FCSTD DOCUMENT  (FreeCAD 0.19R24276 (Git))
Label: Master_sketch_3_3
License: All rights reserved
LicenseURL: http://en.wikipedia.org/wiki/All_rights_reserved
objects: Sketcher::SketchObject×1, PartDesign::Body×1
note: 2 computed .brp shape members not serialized (recipe doc carries the construction recipe); baked Part::Feature solids carry a one-line shape summary decoded from their .brp

FEATURE [Sketcher::SketchObject] Sketch
  FullyConstrained = false
  MapMode = 5
  Support = -> [XY_Plane]
  sketch-geometry (226):
    g0: LineSegment StartX=-40 StartY=82 StartZ=0 EndX=40 EndY=82 EndZ=0
    g1: LineSegment StartX=40 StartY=82 StartZ=0 EndX=40 EndY=71 EndZ=0
    g2: LineSegment StartX=40 StartY=71 StartZ=0 EndX=-40 EndY=71 EndZ=0
    g3: LineSegment StartX=-40 StartY=71 StartZ=0 EndX=-40 EndY=82 EndZ=0
    g4: LineSegment StartX=-25 StartY=82 StartZ=0 EndX=-25 EndY=71 EndZ=0
    g5: LineSegment StartX=25 StartY=82 StartZ=0 EndX=25 EndY=71 EndZ=0
    g6: LineSegment StartX=-40 StartY=71 StartZ=0 EndX=-25 EndY=82 EndZ=0
    g7: LineSegment StartX=-40 StartY=82 StartZ=0 EndX=-25 EndY=71 EndZ=0
    g8: LineSegment StartX=25 StartY=71 StartZ=0 EndX=40 EndY=82 EndZ=0
    g9: LineSegment StartX=25 StartY=82 StartZ=0 EndX=40 EndY=71 EndZ=0
    g10: LineSegment StartX=-40 StartY=104 StartZ=0 EndX=40 EndY=104 EndZ=0
    g11: LineSegment StartX=40 StartY=104 StartZ=0 EndX=40 EndY=115 EndZ=0
    g12: LineSegment StartX=40 StartY=115 StartZ=0 EndX=-40 EndY=115 EndZ=0
    g13: LineSegment StartX=-40 StartY=115 StartZ=0 EndX=-40 EndY=104 EndZ=0
    g14: LineSegment StartX=-25 StartY=104 StartZ=0 EndX=-25 EndY=115 EndZ=0
    g15: LineSegment StartX=25 StartY=104 StartZ=0 EndX=25 EndY=115 EndZ=0
    g16: LineSegment StartX=-40 StartY=115 StartZ=0 EndX=-25 EndY=104 EndZ=0
    g17: LineSegment StartX=-40 StartY=104 StartZ=0 EndX=-25 EndY=115 EndZ=0
    g18: LineSegment StartX=25 StartY=115 StartZ=0 EndX=40 EndY=104 EndZ=0
    g19: LineSegment StartX=25 StartY=104 StartZ=0 EndX=40 EndY=115 EndZ=0
    g20: LineSegment StartX=-116.97 StartY=92 StartZ=0 EndX=25 EndY=92 EndZ=0
    g21: LineSegment StartX=25 StartY=92 StartZ=0 EndX=25 EndY=86 EndZ=0
    g22: LineSegment StartX=25 StartY=86 StartZ=0 EndX=-116.97 EndY=86 EndZ=0
    g23: LineSegment StartX=-116.97 StartY=86 StartZ=0 EndX=-116.97 EndY=92 EndZ=0
    g24: LineSegment StartX=-24 StartY=116 StartZ=0 EndX=-13 EndY=116 EndZ=0
    g25: LineSegment StartX=24 StartY=116 StartZ=0 EndX=24 EndY=70 EndZ=0
    g26: LineSegment StartX=24 StartY=70 StartZ=0 EndX=-24 EndY=70 EndZ=0
    g27: LineSegment StartX=61.35 StartY=170 StartZ=0 EndX=61.35 EndY=10 EndZ=0
    g28: LineSegment StartX=44.35 StartY=70 StartZ=0 EndX=44.35 EndY=98 EndZ=0
    g29: LineSegment StartX=26.35 StartY=70 StartZ=0 EndX=44.35 EndY=70 EndZ=0
    g30: LineSegment StartX=26.35 StartY=103 StartZ=0 EndX=44.35 EndY=103 EndZ=0
    g31: LineSegment StartX=44.35 StartY=98 StartZ=0 EndX=26.35 EndY=98 EndZ=0
    g32: LineSegment StartX=26.35 StartY=98 StartZ=0 EndX=26.35 EndY=103 EndZ=0
    g33: LineSegment StartX=44.35 StartY=103 StartZ=0 EndX=44.35 EndY=123 EndZ=0
    g34: LineSegment StartX=-115.97 StartY=94 StartZ=0 EndX=-99.97 EndY=94 EndZ=0
    g35: LineSegment StartX=-99.97 StartY=94 StartZ=0 EndX=-99.97 EndY=84 EndZ=0
    g36: LineSegment StartX=-99.97 StartY=84 StartZ=0 EndX=-115.97 EndY=84 EndZ=0
    g37: LineSegment StartX=-115.97 StartY=84 StartZ=0 EndX=-115.97 EndY=94 EndZ=0
    g38: LineSegment StartX=-110.97 StartY=84 StartZ=0 EndX=-104.97 EndY=84 EndZ=0
    g39: LineSegment StartX=-104.97 StartY=84 StartZ=0 EndX=-104.97 EndY=74 EndZ=0
    g40: LineSegment StartX=-104.97 StartY=74 StartZ=0 EndX=-110.97 EndY=74 EndZ=0
    g41: LineSegment StartX=-110.97 StartY=74 StartZ=0 EndX=-110.97 EndY=84 EndZ=0
    g42: LineSegment StartX=-123.97 StartY=74 StartZ=0 EndX=-91.97 EndY=74 EndZ=0
    g43: LineSegment StartX=-91.97 StartY=74 StartZ=0 EndX=-91.97 EndY=24 EndZ=0
    g44: LineSegment StartX=-91.97 StartY=24 StartZ=0 EndX=-123.97 EndY=24 EndZ=0
    g45: LineSegment StartX=-123.97 StartY=24 StartZ=0 EndX=-123.97 EndY=74 EndZ=0
    g46: LineSegment StartX=-40 StartY=173 StartZ=0 EndX=40 EndY=173 EndZ=0
    g47: LineSegment StartX=40 StartY=173 StartZ=0 EndX=40 EndY=162 EndZ=0
    g48: LineSegment StartX=-40 StartY=162 StartZ=0 EndX=-40 EndY=173 EndZ=0
    g49: LineSegment StartX=-25 StartY=173 StartZ=0 EndX=-25 EndY=162 EndZ=0
    g50: LineSegment StartX=25 StartY=173 StartZ=0 EndX=25 EndY=162 EndZ=0
    g51: LineSegment StartX=-40 StartY=162 StartZ=0 EndX=-25 EndY=173 EndZ=0
    g52: LineSegment StartX=-40 StartY=173 StartZ=0 EndX=-25 EndY=162 EndZ=0
    g53: LineSegment StartX=25 StartY=162 StartZ=0 EndX=40 EndY=173 EndZ=0
    g54: LineSegment StartX=25 StartY=173 StartZ=0 EndX=40 EndY=162 EndZ=0
    g55: LineSegment StartX=26.35 StartY=70 StartZ=0 EndX=26.35 EndY=10 EndZ=0
    g56: LineSegment StartX=26.35 StartY=10 StartZ=0 EndX=61.35 EndY=10 EndZ=0
    g57: LineSegment StartX=-26.35 StartY=70 StartZ=0 EndX=-61.35 EndY=70 EndZ=0
    g58: LineSegment StartX=-61.35 StartY=70 StartZ=0 EndX=-61.35 EndY=10 EndZ=0
    g59: LineSegment StartX=-61.35 StartY=10 StartZ=0 EndX=-26.35 EndY=10 EndZ=0
    g60: LineSegment StartX=-26.35 StartY=10 StartZ=0 EndX=-26.35 EndY=70 EndZ=0
    g61: LineSegment StartX=61.35 StartY=10 StartZ=0 EndX=-238.65 EndY=10 EndZ=0
    g62: LineSegment StartX=-238.65 StartY=10 StartZ=0 EndX=-238.65 EndY=0 EndZ=0
    g63: LineSegment StartX=-238.65 StartY=0 StartZ=0 EndX=61.35 EndY=0 EndZ=0
    g64: LineSegment StartX=61.35 StartY=0 StartZ=0 EndX=61.35 EndY=10 EndZ=0
    g65: LineSegment StartX=110 StartY=227.577 StartZ=0 EndX=190 EndY=227.577 EndZ=0
    g66: LineSegment StartX=190 StartY=227.577 StartZ=0 EndX=190 EndY=238.577 EndZ=0
    g67: LineSegment StartX=190 StartY=238.577 StartZ=0 EndX=110 EndY=238.577 EndZ=0
    g68: LineSegment StartX=110 StartY=238.577 StartZ=0 EndX=110 EndY=227.577 EndZ=0
    g69: LineSegment StartX=125 StartY=227.577 StartZ=0 EndX=125 EndY=238.577 EndZ=0
    g70: LineSegment StartX=175 StartY=227.577 StartZ=0 EndX=175 EndY=238.577 EndZ=0
    g71: LineSegment StartX=110 StartY=238.577 StartZ=0 EndX=125 EndY=227.577 EndZ=0
    g72: LineSegment StartX=110 StartY=227.577 StartZ=0 EndX=125 EndY=238.577 EndZ=0
    g73: LineSegment StartX=175 StartY=238.577 StartZ=0 EndX=190 EndY=227.577 EndZ=0
    g74: LineSegment StartX=175 StartY=227.577 StartZ=0 EndX=190 EndY=238.577 EndZ=0
    g75: LineSegment StartX=0 StartY=0 StartZ=0 EndX=0 EndY=224.141 EndZ=0
    g76: LineSegment StartX=150 StartY=311.289 StartZ=0 EndX=150 EndY=227.577 EndZ=0
    g77: LineSegment StartX=128.455 StartY=216.402 StartZ=0 EndX=171.545 EndY=216.402 EndZ=0
    g78: LineSegment StartX=171.545 StartY=311.289 StartZ=0 EndX=128.455 EndY=311.289 EndZ=0
    g79: LineSegment StartX=128.455 StartY=311.289 StartZ=0 EndX=128.455 EndY=216.402 EndZ=0
    g80: LineSegment StartX=204.13 StartY=225.651 StartZ=0 EndX=204.13 EndY=243.027 EndZ=0
    g81: LineSegment StartX=204.13 StartY=243.027 StartZ=0 EndX=-12.5 EndY=243.027 EndZ=0
    g82: LineSegment StartX=171.545 StartY=311.289 StartZ=0 EndX=171.545 EndY=216.402 EndZ=0
    g83: LineSegment StartX=-190 StartY=228.226 StartZ=0 EndX=-110 EndY=228.226 EndZ=0
    g84: LineSegment StartX=-110 StartY=228.226 StartZ=0 EndX=-110 EndY=239.226 EndZ=0
    g85: LineSegment StartX=-110 StartY=239.226 StartZ=0 EndX=-190 EndY=239.226 EndZ=0
    g86: LineSegment StartX=-190 StartY=239.226 StartZ=0 EndX=-190 EndY=228.226 EndZ=0
    g87: LineSegment StartX=-175 StartY=228.226 StartZ=0 EndX=-175 EndY=239.226 EndZ=0
    g88: LineSegment StartX=-125 StartY=228.226 StartZ=0 EndX=-125 EndY=239.226 EndZ=0
    g89: LineSegment StartX=-190 StartY=239.226 StartZ=0 EndX=-175 EndY=228.226 EndZ=0
    g90: LineSegment StartX=-190 StartY=228.226 StartZ=0 EndX=-175 EndY=239.226 EndZ=0
    g91: LineSegment StartX=-125 StartY=239.226 StartZ=0 EndX=-110 EndY=228.226 EndZ=0
    g92: LineSegment StartX=-125 StartY=228.226 StartZ=0 EndX=-110 EndY=239.226 EndZ=0
    g93: LineSegment StartX=-194.17 StartY=243.027 StartZ=0 EndX=13 EndY=243.027 EndZ=0
    g94: LineSegment StartX=-194.17 StartY=225.651 StartZ=0 EndX=-194.17 EndY=243.027 EndZ=0
    g95: LineSegment StartX=-13 StartY=276 StartZ=0 EndX=13 EndY=276 EndZ=0
    g96: LineSegment StartX=-168.275 StartY=307.347 StartZ=0 EndX=-131.725 EndY=307.347 EndZ=0
    g97: LineSegment StartX=-131.725 StartY=307.347 StartZ=0 EndX=-131.725 EndY=215.705 EndZ=0
    g98: LineSegment StartX=-131.725 StartY=215.705 StartZ=0 EndX=-168.275 EndY=215.705 EndZ=0
    g99: LineSegment StartX=-168.275 StartY=215.705 StartZ=0 EndX=-168.275 EndY=307.347 EndZ=0
    g100: LineSegment StartX=-150 StartY=228.226 StartZ=0 EndX=-150 EndY=307.347 EndZ=0
    g101: LineSegment StartX=40 StartY=162 StartZ=0 EndX=-40 EndY=162 EndZ=0
    g102: LineSegment StartX=-107.97 StartY=74 StartZ=0 EndX=-107.97 EndY=24 EndZ=0
    g103: LineSegment StartX=-107.97 StartY=74 StartZ=0 EndX=-107.97 EndY=84 EndZ=0
    g104: LineSegment StartX=-178 StartY=158 StartZ=0 EndX=-162 EndY=158 EndZ=0
    g105: LineSegment StartX=-162 StartY=158 StartZ=0 EndX=-162 EndY=148 EndZ=0
    g106: LineSegment StartX=-162 StartY=148 StartZ=0 EndX=-178 EndY=148 EndZ=0
    g107: LineSegment StartX=-178 StartY=148 StartZ=0 EndX=-178 EndY=158 EndZ=0
    g108: LineSegment StartX=-173 StartY=148 StartZ=0 EndX=-167 EndY=148 EndZ=0
    g109: LineSegment StartX=-167 StartY=148 StartZ=0 EndX=-167 EndY=138 EndZ=0
    g110: LineSegment StartX=-167 StartY=138 StartZ=0 EndX=-173 EndY=138 EndZ=0
    g111: LineSegment StartX=-173 StartY=138 StartZ=0 EndX=-173 EndY=148 EndZ=0
    g112: LineSegment StartX=-186 StartY=138 StartZ=0 EndX=-154 EndY=138 EndZ=0
    g113: LineSegment StartX=-154 StartY=138 StartZ=0 EndX=-154 EndY=88 EndZ=0
    g114: LineSegment StartX=-154 StartY=88 StartZ=0 EndX=-186 EndY=88 EndZ=0
    g115: LineSegment StartX=-186 StartY=88 StartZ=0 EndX=-186 EndY=138 EndZ=0
    g116: LineSegment StartX=-170 StartY=138 StartZ=0 EndX=-170 EndY=88 EndZ=0
    g117: LineSegment StartX=-170 StartY=111.828 StartZ=0 EndX=-170 EndY=148 EndZ=0
    g118: LineSegment StartX=-180 StartY=150 StartZ=0 EndX=-180 EndY=156 EndZ=0
    g119: LineSegment StartX=-24 StartY=70 StartZ=0 EndX=-24 EndY=116 EndZ=0
    g120: LineSegment StartX=-40 StartY=140 StartZ=0 EndX=40 EndY=140 EndZ=0
    g121: LineSegment StartX=40 StartY=140 StartZ=0 EndX=40 EndY=129 EndZ=0
    g122: LineSegment StartX=40 StartY=129 StartZ=0 EndX=-40 EndY=129 EndZ=0
    g123: LineSegment StartX=-40 StartY=129 StartZ=0 EndX=-40 EndY=140 EndZ=0
    g124: LineSegment StartX=-25 StartY=140 StartZ=0 EndX=-25 EndY=129 EndZ=0
    g125: LineSegment StartX=25 StartY=140 StartZ=0 EndX=25 EndY=129 EndZ=0
    g126: LineSegment StartX=-40 StartY=129 StartZ=0 EndX=-25 EndY=140 EndZ=0
    g127: LineSegment StartX=-40 StartY=140 StartZ=0 EndX=-25 EndY=129 EndZ=0
    g128: LineSegment StartX=25 StartY=129 StartZ=0 EndX=40 EndY=140 EndZ=0
    g129: LineSegment StartX=25 StartY=140 StartZ=0 EndX=40 EndY=129 EndZ=0
    g130: LineSegment StartX=44.35 StartY=123 StartZ=0 EndX=26.35 EndY=123 EndZ=0
    g131: LineSegment StartX=26.35 StartY=123 StartZ=0 EndX=26.35 EndY=128 EndZ=0
    g132: LineSegment StartX=26.35 StartY=128 StartZ=0 EndX=44.35 EndY=128 EndZ=0
    g133: LineSegment StartX=44.35 StartY=128 StartZ=0 EndX=44.35 EndY=156 EndZ=0
    g134: LineSegment StartX=44.35 StartY=170 StartZ=0 EndX=61.35 EndY=170 EndZ=0
    g135: LineSegment StartX=0 StartY=0 StartZ=0 EndX=0 EndY=116 EndZ=0
    g136: LineSegment StartX=13 StartY=116 StartZ=0 EndX=24 EndY=116 EndZ=0
    g137: LineSegment StartX=20 StartY=140 StartZ=0 EndX=20 EndY=129 EndZ=0
    g138: LineSegment StartX=18.3275 StartY=125.289 StartZ=0 EndX=13.9148 EndY=125.289 EndZ=0
    g139: LineSegment StartX=13.9148 StartY=125.289 StartZ=0 EndX=13.9148 EndY=256.464 EndZ=0
    g140: LineSegment StartX=18.3275 StartY=125.289 StartZ=0 EndX=-17.323 EndY=125.289 EndZ=0
    g141: LineSegment StartX=-17.323 StartY=125.289 StartZ=0 EndX=-17.323 EndY=256.464 EndZ=0
    g142: LineSegment StartX=18.3275 StartY=256.464 StartZ=0 EndX=18.3275 EndY=125.289 EndZ=0
    g143: LineSegment StartX=-180 StartY=156 StartZ=0 EndX=19.8909 EndY=156 EndZ=0
    g144: LineSegment StartX=19.8909 StartY=156 StartZ=0 EndX=19.8909 EndY=150 EndZ=0
    g145: LineSegment StartX=19.8909 StartY=150 StartZ=0 EndX=-180 EndY=150 EndZ=0
    g146: LineSegment StartX=-180 StartY=150 StartZ=0 EndX=-180 EndY=156 EndZ=0
    g147: LineSegment StartX=-21.344 StartY=253.141 StartZ=0 EndX=172.767 EndY=253.141 EndZ=0
    g148: LineSegment StartX=172.767 StartY=253.141 StartZ=0 EndX=172.767 EndY=247.025 EndZ=0
    g149: LineSegment StartX=172.767 StartY=247.025 StartZ=0 EndX=-21.344 EndY=247.025 EndZ=0
    g150: LineSegment StartX=-21.344 StartY=247.025 StartZ=0 EndX=-21.344 EndY=253.141 EndZ=0
    g151: LineSegment StartX=-170 StartY=274 StartZ=0 EndX=15 EndY=274 EndZ=0
    g152: LineSegment StartX=15 StartY=274 StartZ=0 EndX=15 EndY=268 EndZ=0
    g153: LineSegment StartX=15 StartY=268 StartZ=0 EndX=-170 EndY=268 EndZ=0
    g154: LineSegment StartX=-170 StartY=268 StartZ=0 EndX=-170 EndY=274 EndZ=0
    g155: LineSegment StartX=-266.032 StartY=241.799 StartZ=0 EndX=-250.032 EndY=241.799 EndZ=0
    g156: LineSegment StartX=-250.032 StartY=241.799 StartZ=0 EndX=-250.032 EndY=231.799 EndZ=0
    g157: LineSegment StartX=-250.032 StartY=231.799 StartZ=0 EndX=-266.032 EndY=231.799 EndZ=0
    g158: LineSegment StartX=-266.032 StartY=231.799 StartZ=0 EndX=-266.032 EndY=241.799 EndZ=0
    g159: LineSegment StartX=-261.032 StartY=231.799 StartZ=0 EndX=-255.032 EndY=231.799 EndZ=0
    g160: LineSegment StartX=-255.032 StartY=231.799 StartZ=0 EndX=-255.032 EndY=221.799 EndZ=0
    g161: LineSegment StartX=-255.032 StartY=221.799 StartZ=0 EndX=-261.032 EndY=221.799 EndZ=0
    g162: LineSegment StartX=-261.032 StartY=221.799 StartZ=0 EndX=-261.032 EndY=231.799 EndZ=0
    g163: LineSegment StartX=-274.032 StartY=221.799 StartZ=0 EndX=-242.032 EndY=221.799 EndZ=0
    g164: LineSegment StartX=-242.032 StartY=221.799 StartZ=0 EndX=-242.032 EndY=171.799 EndZ=0
    g165: LineSegment StartX=-242.032 StartY=171.799 StartZ=0 EndX=-274.032 EndY=171.799 EndZ=0
    g166: LineSegment StartX=-274.032 StartY=171.799 StartZ=0 EndX=-274.032 EndY=221.799 EndZ=0
    g167: LineSegment StartX=-258.032 StartY=221.799 StartZ=0 EndX=-258.032 EndY=171.799 EndZ=0
    g168: LineSegment StartX=-258.032 StartY=157.127 StartZ=0 EndX=-258.032 EndY=231.799 EndZ=0
    g169: LineSegment StartX=-268.032 StartY=233.799 StartZ=0 EndX=-268.032 EndY=239.799 EndZ=0
    g170: LineSegment StartX=-268.032 StartY=239.799 StartZ=0 EndX=-192.409 EndY=239.799 EndZ=0
    g171: LineSegment StartX=-268.032 StartY=233.799 StartZ=0 EndX=-192.409 EndY=233.799 EndZ=0
    g172: LineSegment StartX=-192.409 StartY=239.799 StartZ=0 EndX=-192.409 EndY=233.799 EndZ=0
    g173: LineSegment StartX=-3.10679 StartY=290.305 StartZ=0 EndX=3.84866 EndY=290.305 EndZ=0
    g174: LineSegment StartX=3.84866 StartY=290.305 StartZ=0 EndX=3.84866 EndY=282.403 EndZ=0
    g175: LineSegment StartX=3.84866 StartY=282.403 StartZ=0 EndX=-3.10679 EndY=282.403 EndZ=0
    g176: LineSegment StartX=-3.10679 StartY=282.403 StartZ=0 EndX=-3.10679 EndY=290.305 EndZ=0
    g177: LineSegment StartX=-153.066 StartY=215.705 StartZ=0 EndX=-145.455 EndY=215.705 EndZ=0
    g178: LineSegment StartX=-145.455 StartY=215.705 StartZ=0 EndX=-145.455 EndY=205.455 EndZ=0
    g179: LineSegment StartX=-145.455 StartY=205.455 StartZ=0 EndX=-153.066 EndY=205.455 EndZ=0
    g180: LineSegment StartX=-153.066 StartY=205.455 StartZ=0 EndX=-153.066 EndY=215.705 EndZ=0
    g181: LineSegment StartX=-150.011 StartY=203.936 StartZ=0 EndX=-132.927 EndY=183.815 EndZ=0
    g182: LineSegment StartX=-132.927 StartY=183.815 StartZ=0 EndX=-96.1008 EndY=203.936 EndZ=0
    g183: LineSegment StartX=-96.1008 StartY=203.936 StartZ=0 EndX=-71.0652 EndY=308.756 EndZ=0
    g184: LineSegment StartX=-71.0652 StartY=308.756 StartZ=0 EndX=-11.3858 EndY=308.756 EndZ=0
    g185: LineSegment StartX=-11.3858 StartY=308.756 StartZ=0 EndX=-0.320477 EndY=291.237 EndZ=0
    g186: LineSegment StartX=154.85 StartY=216.402 StartZ=0 EndX=145.682 EndY=216.402 EndZ=0
    g187: LineSegment StartX=145.682 StartY=216.402 StartZ=0 EndX=145.682 EndY=202.462 EndZ=0
    g188: LineSegment StartX=145.682 StartY=202.462 StartZ=0 EndX=154.85 EndY=202.462 EndZ=0
    g189: LineSegment StartX=154.85 StartY=202.462 StartZ=0 EndX=154.85 EndY=216.402 EndZ=0
    g190: LineSegment StartX=-0.320477 StartY=291.237 StartZ=0 EndX=16.5786 EndY=307.914 EndZ=0
    g191: LineSegment StartX=16.5786 StartY=307.914 StartZ=0 EndX=62.4853 EndY=307.914 EndZ=0
    g192: LineSegment StartX=62.4853 StartY=307.914 StartZ=0 EndX=113.808 EndY=191.418 EndZ=0
    g193: LineSegment StartX=113.808 StartY=191.418 StartZ=0 EndX=141.779 EndY=181.787 EndZ=0
    g194: LineSegment StartX=141.779 StartY=181.787 StartZ=0 EndX=149.543 EndY=200.402 EndZ=0
    g195: LineSegment StartX=44.35 StartY=161 StartZ=0 EndX=26.35 EndY=161 EndZ=0
    g196: LineSegment StartX=26.35 StartY=161 StartZ=0 EndX=26.35 EndY=156 EndZ=0
    g197: LineSegment StartX=44.35 StartY=161 StartZ=0 EndX=44.35 EndY=170 EndZ=0
    g198: LineSegment StartX=44.35 StartY=156 StartZ=0 EndX=26.35 EndY=156 EndZ=0
    g199: LineSegment StartX=-13 StartY=116 StartZ=0 EndX=-13 EndY=276 EndZ=0
    g200: LineSegment StartX=13 StartY=116 StartZ=0 EndX=13 EndY=276 EndZ=0
    g201: LineSegment StartX=-194.17 StartY=225.651 StartZ=0 EndX=204.13 EndY=225.651 EndZ=0
    g202: LineSegment StartX=-40 StartY=261.408 StartZ=0 EndX=40 EndY=261.408 EndZ=0
    g203: LineSegment StartX=40 StartY=261.408 StartZ=0 EndX=40 EndY=272.408 EndZ=0
    g204: LineSegment StartX=-40 StartY=272.408 StartZ=0 EndX=-40 EndY=261.408 EndZ=0
    g205: LineSegment StartX=-25 StartY=261.408 StartZ=0 EndX=-25 EndY=272.408 EndZ=0
    g206: LineSegment StartX=25 StartY=261.408 StartZ=0 EndX=25 EndY=272.408 EndZ=0
    g207: LineSegment StartX=-40 StartY=272.408 StartZ=0 EndX=-25 EndY=261.408 EndZ=0
    g208: LineSegment StartX=-40 StartY=261.408 StartZ=0 EndX=-25 EndY=272.408 EndZ=0
    g209: LineSegment StartX=25 StartY=272.408 StartZ=0 EndX=40 EndY=261.408 EndZ=0
    g210: LineSegment StartX=25 StartY=261.408 StartZ=0 EndX=40 EndY=272.408 EndZ=0
    g211: LineSegment StartX=40 StartY=272.408 StartZ=0 EndX=-40 EndY=272.408 EndZ=0
    g212: LineSegment StartX=-50.3828 StartY=256.464 StartZ=0 EndX=-17.323 EndY=256.464 EndZ=0
    g213: LineSegment StartX=49.155 StartY=256.464 StartZ=0 EndX=49.155 EndY=272.88 EndZ=0
    g214: LineSegment StartX=49.155 StartY=272.88 StartZ=0 EndX=-50.3828 EndY=272.88 EndZ=0
    g215: LineSegment StartX=-50.3828 StartY=272.88 StartZ=0 EndX=-50.3828 EndY=256.464 EndZ=0
    g216: LineSegment StartX=0 StartY=224.141 StartZ=0 EndX=0 EndY=261.408 EndZ=0
    g217: LineSegment StartX=13.9148 StartY=256.464 StartZ=0 EndX=49.155 EndY=256.464 EndZ=0
    g218: LineSegment StartX=-25 StartY=270.823 StartZ=0 EndX=-13.6623 EndY=270.823 EndZ=0
    g219: LineSegment StartX=-13.6623 StartY=270.823 StartZ=0 EndX=-13.6623 EndY=262.818 EndZ=0
    g220: LineSegment StartX=-13.6623 StartY=262.818 StartZ=0 EndX=-25 EndY=262.818 EndZ=0
    g221: LineSegment StartX=-25 StartY=262.818 StartZ=0 EndX=-25 EndY=270.823 EndZ=0
    g222: LineSegment StartX=14.0101 StartY=270.823 StartZ=0 EndX=25 EndY=270.823 EndZ=0
    g223: LineSegment StartX=25 StartY=270.823 StartZ=0 EndX=25 EndY=262.818 EndZ=0
    g224: LineSegment StartX=25 StartY=262.818 StartZ=0 EndX=14.0101 EndY=262.818 EndZ=0
    g225: LineSegment StartX=14.0101 StartY=262.818 StartZ=0 EndX=14.0101 EndY=270.823 EndZ=0
  constraints (591):
    c: Coincident(g0,g1)
    c: Coincident(g1,g2)
    c: Coincident(g2,g3)
    c: Coincident(g3,g0)
    c: Horizontal(g0)
    c: Horizontal(g2)
    c: Vertical(g1)
    c: Vertical(g3)
    c: PointOnObject(g4,g0)
    c: PointOnObject(g4,g2)
    c: Vertical(g4)
    c: PointOnObject(g5,g0)
    c: Vertical(g5)
    c: DistanceX(g2,g2) = 80
    c: DistanceX(g4,g5) = 50
    c: DistanceY(g3,g3) = 11
    c: Coincident(g6,g2)
    c: Coincident(g6,g4)
    c: Coincident(g7,g0)
    c: Coincident(g7,g4)
    c: Coincident(g8,g5)
    c: Coincident(g8,g0)
    c: Coincident(g9,g5)
    c: Coincident(g9,g1)
    c: DistanceX(g2,g4) = 15
    c: Coincident(g10,g11)
    c: Coincident(g11,g12)
    c: Coincident(g12,g13)
    c: Coincident(g13,g10)
    c: Horizontal(g10)
    c: Horizontal(g12)
    c: Vertical(g11)
    c: Vertical(g13)
    c: PointOnObject(g14,g10)
    c: PointOnObject(g14,g12)
    c: Vertical(g14)
    c: PointOnObject(g15,g10)
    c: Vertical(g15)
    c: Coincident(g16,g12)
    c: Coincident(g16,g14)
    c: Coincident(g17,g10)
    c: Coincident(g17,g14)
    c: Coincident(g18,g15)
    c: Coincident(g18,g10)
    c: Coincident(g19,g15)
    c: Coincident(g19,g11)
    c: Equal(g10,g2)
    c: Equal(g1,g11)
    c: Equal(g15,g11)
    c: Equal(g16,g7)
    c: Equal(g19,g8)
    c: Horizontal(g5,g1)
    c: Vertical(g4,g14)
    c: Coincident(g20,g21)
    c: Coincident(g21,g22)
    c: Coincident(g22,g23)
    c: Coincident(g23,g20)
    c: Horizontal(g20)
    c: Horizontal(g22)
    c: Vertical(g21)
    c: Vertical(g23)
    c: Coincident(g25,g26)
    c: Horizontal(g24)
    c: Horizontal(g26)
    c: Vertical(g25)
    c: DistanceX(g4,g26) = 1
    c: Vertical(g27)
    c: Vertical(g28)
    c: Horizontal(g29)
    c: Coincident(g31,g32)
    c: Coincident(g32,g30)
    c: Horizontal(g30)
    c: Horizontal(g31)
    c: Vertical(g32)
    c: Tangent(g28,g33)
    c: Vertical(g29,g31)
    c: Coincident(g29,g28)
    c: Coincident(g28,g31)
    c: Coincident(g30,g33)
    c: Coincident(g34,g35)
    c: Coincident(g35,g36)
    c: Coincident(g36,g37)
    c: Coincident(g37,g34)
    c: Horizontal(g34)
    c: Horizontal(g36)
    c: Vertical(g35)
    c: Vertical(g37)
    c: Coincident(g38,g39)
    c: Coincident(g39,g40)
    c: Coincident(g40,g41)
    c: Coincident(g41,g38)
    c: Horizontal(g38)
    c: Horizontal(g40)
    c: Vertical(g39)
    c: Vertical(g41)
    c: PointOnObject(g38,g36)
    c: Coincident(g42,g43)
    c: Coincident(g43,g44)
    c: Coincident(g44,g45)
    c: Coincident(g45,g42)
    c: Horizontal(g42)
    c: Horizontal(g44)
    c: Vertical(g43)
    c: Vertical(g45)
    c: Coincident(g101,g48)
    c: Coincident(g48,g46)
    c: Horizontal(g46)
    c: Vertical(g47)
    c: Vertical(g48)
    c: PointOnObject(g49,g46)
    c: Vertical(g49)
    c: PointOnObject(g50,g46)
    c: Vertical(g50)
    c: Coincident(g51,g101)
    c: Coincident(g51,g49)
    c: Coincident(g52,g46)
    c: Coincident(g52,g49)
    c: Coincident(g53,g50)
    c: Coincident(g54,g50)
    c: Coincident(g54,g47)
    c: Equal(g50,g47)
    c: Vertical(g101,g0)
    c: DistanceX(g5,g29) = 1.35
    c: DistanceX(g29,g29) = 18
    c: DistanceY(g28,g1) = 1
    c: DistanceY(g30,g10) = 1
    c: DistanceX(g25,g21) = 1
    c: DistanceX(g22,g36) = 1
    c: Coincident(g55,g56)
    c: Horizontal(g56)
    c: Vertical(g55)
    c: Coincident(g57,g58)
    c: Coincident(g58,g59)
    c: Coincident(g59,g60)
    c: Coincident(g60,g57)
    c: Horizontal(g57)
    c: Horizontal(g59)
    c: Vertical(g58)
    c: Vertical(g60)
    c: Horizontal(g59,g55)
    c: Equal(g59,g56)
    c: Coincident(g61,g62)
    c: Coincident(g62,g63)
    c: Coincident(g63,g64)
    c: Coincident(g64,g61)
    c: Horizontal(g61)
    c: Horizontal(g63)
    c: Vertical(g62)
    c: Vertical(g64)
    c: Coincident(g61,g56)
    c: Coincident(g65,g66)
    c: Coincident(g66,g67)
    c: Coincident(g67,g68)
    c: Coincident(g68,g65)
    c: Horizontal(g65)
    c: Vertical(g66)
    c: Vertical(g68)
    c: PointOnObject(g69,g65)
    c: PointOnObject(g69,g67)
    c: Vertical(g69)
    c: PointOnObject(g70,g65)
    c: Vertical(g70)
    c: Coincident(g71,g67)
    c: Coincident(g71,g69)
    c: Coincident(g72,g65)
    c: Coincident(g72,g69)
    c: Coincident(g73,g70)
    c: Coincident(g73,g65)
    c: Coincident(g74,g70)
    c: Coincident(g74,g66)
    c: Equal(g70,g66)
    c: Equal(g66,g47)
    c: Equal(g47,g68)
    c: Parallel(g74,g53)
    c: Parallel(g71,g52)
    c: Vertical(g75)
    c: Vertical(g76)
    c: Symmetric(g65,g65,g76)
    c: DistanceX(g75,g76) = 150
    c: DistanceX(g57,g4) = 1.35
    c: Coincident(g78,g79)
    c: Coincident(g79,g77)
    c: Horizontal(g77)
    c: Horizontal(g78)
    c: Vertical(g79)
    c: Coincident(g80,g81)
    c: Horizontal(g81)
    c: Vertical(g80)
    c: Vertical(g82)
    c: Coincident(g82,g77)
    c: Coincident(g78,g82)
    c: Horizontal(g57,g29)
    c: Coincident(g83,g84)
    c: Coincident(g84,g85)
    c: Coincident(g85,g86)
    c: Coincident(g86,g83)
    c: Horizontal(g83)
    c: Horizontal(g85)
    c: Vertical(g84)
    c: Vertical(g86)
    c: PointOnObject(g87,g83)
    c: PointOnObject(g87,g85)
    c: Vertical(g87)
    c: PointOnObject(g88,g83)
    c: Vertical(g88)
    c: Coincident(g89,g85)
    c: Coincident(g89,g87)
    c: Coincident(g90,g83)
    c: Coincident(g90,g87)
    c: Coincident(g91,g88)
    c: Coincident(g91,g83)
    c: Coincident(g92,g88)
    c: Coincident(g92,g84)
    c: Equal(g88,g84)
    c: Equal(g84,g47)
    c: Parallel(g92,g53)
    c: Parallel(g90,g51)
    c: Coincident(g94,g93)
    c: Horizontal(g93)
    c: Vertical(g94)
    c: Horizontal(g95)
    c: Vertical(g93,g95)
    c: Coincident(g96,g97)
    c: Coincident(g97,g98)
    c: Coincident(g98,g99)
    c: Coincident(g99,g96)
    c: Horizontal(g96)
    c: Horizontal(g98)
    c: Vertical(g97)
    c: Vertical(g99)
    c: Vertical(g100)
    c: Symmetric(g83,g83,g100)
    c: Symmetric(g96,g96,g100)
    c: DistanceX(g100,g75) = 150
    c: Symmetric(g78,g78,g76)
    c: Vertical(g102)
    c: Symmetric(g44,g43,g102)
    c: Symmetric(g40,g39,g102)
    c: DistanceX(g44,g44) = 32
    c: Coincident(g103,g102)
    c: Vertical(g103)
    c: Symmetric(g36,g35,g103)
    c: DistanceX(g102,g75) = 107.97
    c: DistanceX(g63,g63) = 300
    c: DistanceX(g77,g77) = 43.09
    c: DistanceX(g98,g98) = 36.55
    c: DistanceX(g66,g80) = 14.13
    c: DistanceX(g94,g83) = 4.17
    c: Coincident(g75,g-1)
    c: DistanceX(g67,g67) = 80
    c: Horizontal(g63,g-1)
    c: DistanceY(g64,g64) = 10
    c: DistanceY(g58,g58) = 60
    c: Coincident(g55,g29)
    c: DistanceX(g58,g59) = 35
    c: DistanceY(g45,g45) = 50
    c: DistanceY(g-1,g102) = 24
    c: Horizontal(g40,g42)
    c: DistanceX(g40,g39) = 6
    c: DistanceX(g36,g36) = 16
    c: DistanceY(g42,g36) = 10
    c: DistanceY(g37,g37) = 10
    c: DistanceY(g23,g23) = 6
    c: Coincident(g104,g105)
    c: Coincident(g105,g106)
    c: Coincident(g106,g107)
    c: Coincident(g107,g104)
    c: Horizontal(g104)
    c: Horizontal(g106)
    c: Vertical(g105)
    c: Vertical(g107)
    c: Coincident(g108,g109)
    c: Coincident(g109,g110)
    c: Coincident(g110,g111)
    c: Coincident(g111,g108)
    c: Horizontal(g108)
    c: Horizontal(g110)
    c: Vertical(g109)
    c: Vertical(g111)
    c: PointOnObject(g108,g106)
    c: Coincident(g112,g113)
    c: Coincident(g113,g114)
    c: Coincident(g114,g115)
    c: Coincident(g115,g112)
    c: Horizontal(g112)
    c: Horizontal(g114)
    c: Vertical(g113)
    c: Vertical(g115)
    c: Vertical(g116)
    c: Symmetric(g114,g113,g116)
    c: Symmetric(g110,g109,g116)
    c: Equal(g44,g114) = 32
    c: Vertical(g117)
    c: Symmetric(g106,g105,g117)
    c: Equal(g45,g115) = 50
    c: Horizontal(g110,g112)
    c: DistanceX(g110,g109) = 6
    c: Equal(g36,g106) = 16
    c: DistanceY(g112,g106) = 10
    c: Equal(g37,g107) = 10
    c: Vertical(g117,g116)
    c: Vertical(g118)
    c: DistanceY(g118,g118) = 6
    c: DistanceY(g106,g118) = 2
    c: DistanceX(g116,g-1) = 170
    c: DistanceX(g118,g104) = 2
    c: DistanceY(g-1,g116) = 88
    c: Coincident(g56,g27)
    c: DistanceY(g27,g27) = 160
    c: DistanceY(g28,g28) = 28
    c: DistanceY(g33,g33) = 20
    c: DistanceY(g32,g32) = 5
    c: DistanceX(g26,g26) = 48
    c: DistanceY(g25,g25) = 46
    c: Horizontal(g25,g29)
    c: Coincident(g119,g26)
    c: Coincident(g119,g24)
    c: Vertical(g119)
    c: DistanceY(g36,g22) = 2
    c: Coincident(g120,g121)
    c: Coincident(g121,g122)
    c: Coincident(g122,g123)
    c: Coincident(g123,g120)
    c: Horizontal(g120)
    c: Horizontal(g122)
    c: Vertical(g121)
    c: Vertical(g123)
    c: PointOnObject(g124,g120)
    c: PointOnObject(g124,g122)
    c: Vertical(g124)
    c: PointOnObject(g125,g120)
    c: Vertical(g125)
    c: Coincident(g126,g122)
    c: Coincident(g126,g124)
    c: Coincident(g127,g120)
    c: Coincident(g127,g124)
    c: Coincident(g128,g125)
    c: Coincident(g128,g120)
    c: Coincident(g129,g125)
    c: Coincident(g129,g121)
    c: Equal(g125,g121)
    c: Equal(g123,g13)
    c: Equal(g122,g10)
    c: Vertical(g122,g12)
    c: Equal(g126,g17)
    c: Equal(g128,g19)
    c: Coincident(g101,g47)
    c: Coincident(g46,g47)
    c: Coincident(g53,g46)
    c: Equal(g53,g128)
    c: Equal(g51,g126)
    c: Equal(g121,g47)
    c: Equal(g101,g122)
    c: Horizontal(g101)
    c: Coincident(g130,g131)
    c: Coincident(g131,g132)
    c: Horizontal(g130)
    c: Horizontal(g132)
    c: Vertical(g131)
    c: Coincident(g130,g33)
    c: Vertical(g130,g30)
    c: Equal(g32,g131)
    c: Coincident(g133,g132)
    c: Vertical(g133)
    c: Coincident(g134,g197)
    c: Coincident(g134,g27)
    c: Horizontal(g134)
    c: Vertical(g132,g33)
    c: DistanceY(g131,g121) = 1
    c: Coincident(g135,g-1)
    c: Symmetric(g24,g25,g135)
    c: Coincident(g136,g25)
    c: Vertical(g137)
    c: PointOnObject(g137,g120)
    c: PointOnObject(g137,g122)
    c: DistanceX(g137,g125) = 5
    c: Coincident(g138,g139)
    c: Horizontal(g138)
    c: Vertical(g139)
    c: Coincident(g140,g141)
    c: Coincident(g142,g140)
    c: Horizontal(g140)
    c: Vertical(g141)
    c: Coincident(g140,g138)
    c: Coincident(g143,g144)
    c: Coincident(g144,g145)
    c: Coincident(g145,g146)
    c: Coincident(g146,g143)
    c: Horizontal(g143)
    c: Horizontal(g145)
    c: Vertical(g144)
    c: Coincident(g143,g118)
    c: Coincident(g145,g118)
    c: Horizontal(g48,g49)
    c: Coincident(g147,g148)
    c: Coincident(g148,g149)
    c: Coincident(g149,g150)
    c: Coincident(g150,g147)
    c: Horizontal(g147)
    c: Horizontal(g149)
    c: Vertical(g148)
    c: Vertical(g150)
    c: Coincident(g151,g152)
    c: Coincident(g152,g153)
    c: Coincident(g153,g154)
    c: Coincident(g154,g151)
    c: Horizontal(g151)
    c: Horizontal(g153)
    c: Vertical(g152)
    c: Vertical(g154)
    c: Coincident(g155,g156)
    c: Coincident(g156,g157)
    c: Coincident(g157,g158)
    c: Coincident(g158,g155)
    c: Horizontal(g155)
    c: Horizontal(g157)
    c: Vertical(g156)
    c: Vertical(g158)
    c: Coincident(g159,g160)
    c: Coincident(g160,g161)
    c: Coincident(g161,g162)
    c: Coincident(g162,g159)
    c: Horizontal(g159)
    c: Horizontal(g161)
    c: Vertical(g160)
    c: Vertical(g162)
    c: PointOnObject(g159,g157)
    c: Coincident(g163,g164)
    c: Coincident(g164,g165)
    c: Coincident(g165,g166)
    c: Coincident(g166,g163)
    c: Horizontal(g163)
    c: Horizontal(g165)
    c: Vertical(g164)
    c: Vertical(g166)
    c: Vertical(g167)
    c: Symmetric(g165,g164,g167)
    c: Symmetric(g161,g160,g167)
    c: Vertical(g168)
    c: Symmetric(g157,g156,g168)
    c: Horizontal(g161,g163)
    c: DistanceX(g161,g160) = 6
    c: DistanceY(g163,g157) = 10
    c: Vertical(g168,g167)
    c: Vertical(g169)
    c: Equal(g118,g169) = 6
    c: DistanceY(g157,g169) = 2
    c: DistanceX(g169,g155) = 2
    c: Equal(g164,g115)
    c: Equal(g156,g105)
    c: Equal(g155,g104)
    c: Equal(g165,g112)
    c: Equal(g10,g83)
    c: Coincident(g170,g169)
    c: Horizontal(g170)
    c: Coincident(g171,g169)
    c: Horizontal(g171)
    c: Coincident(g172,g170)
    c: Coincident(g172,g171)
    c: Vertical(g172)
    c: Coincident(g173,g174)
    c: Coincident(g174,g175)
    c: Coincident(g175,g176)
    c: Coincident(g176,g173)
    c: Horizontal(g173)
    c: Horizontal(g175)
    c: Vertical(g174)
    c: Vertical(g176)
    c: Coincident(g177,g178)
    c: Coincident(g178,g179)
    c: Coincident(g179,g180)
    c: Coincident(g180,g177)
    c: Horizontal(g177)
    c: Horizontal(g179)
    c: Vertical(g178)
    c: Vertical(g180)
    c: PointOnObject(g177,g98)
    c: Coincident(g182,g181)
    c: Coincident(g183,g182)
    c: Coincident(g184,g183)
    c: Coincident(g185,g184)
    c: Coincident(g186,g187)
    c: Coincident(g187,g188)
    c: Coincident(g188,g189)
    c: Coincident(g189,g186)
    c: Horizontal(g186)
    c: Horizontal(g188)
    c: Vertical(g187)
    c: Vertical(g189)
    c: PointOnObject(g186,g77)
    c: Coincident(g190,g185)
    c: Coincident(g191,g190)
    c: Horizontal(g191)
    c: Coincident(g192,g191)
    c: Coincident(g193,g192)
    c: Coincident(g194,g193)
    c: Horizontal(g81,g93)
    c: Coincident(g195,g196)
    c: Horizontal(g195)
    c: Vertical(g196)
    c: Vertical(g131,g196)
    c: Equal(g131,g196)
    c: DistanceY(g195,g50) = 1
    c: Coincident(g197,g195)
    c: Tangent(g133,g197)
    c: DistanceY(g195,g134) = 9
    c: Coincident(g198,g133)
    c: Coincident(g198,g196)
    c: Horizontal(g198)
    c: Coincident(g199,g95)
    c: Vertical(g199)
    c: Coincident(g200,g95)
    c: Vertical(g200)
    c: Vertical(g135)
    c: Coincident(g201,g94)
    c: Horizontal(g201)
    c: Coincident(g80,g201)
    c: Coincident(g136,g200)
    c: Coincident(g24,g199)
    c: Symmetric(g24,g136,g135)
    c: DistanceX(g24,g136) = 26
    c: Horizontal(g24,g136)
    c: DistanceY(g200,g200) = 160
    c: DistanceX(g95,g151) = 2
    c: DistanceY(g151,g95) = 2
    c: DistanceY(g152,g152) = 6
    c: DistanceX(g151,g151) = 185
    c: Coincident(g211,g204)
    c: Coincident(g204,g202)
    c: PointOnObject(g205,g202)
    c: PointOnObject(g206,g202)
    c: Coincident(g207,g211)
    c: Coincident(g207,g205)
    c: Coincident(g208,g202)
    c: Coincident(g208,g205)
    c: Coincident(g209,g206)
    c: Coincident(g210,g206)
    c: Coincident(g210,g203)
    c: Equal(g206,g203)
    c: Coincident(g211,g203)
    c: Coincident(g202,g203)
    c: Coincident(g209,g202)
    c: Horizontal(g202)
    c: Horizontal(g211)
    c: Vertical(g203)
    c: Horizontal(g204,g205)
    c: Vertical(g205)
    c: Vertical(g206)
    c: Vertical(g204)
    c: Equal(g46,g202)
    c: Equal(g203,g47)
    c: Equal(g210,g53)
    c: Equal(g208,g210)
    c: Coincident(g217,g213)
    c: Coincident(g213,g214)
    c: Coincident(g214,g215)
    c: Coincident(g215,g212)
    c: Horizontal(g212)
    c: Horizontal(g214)
    c: Vertical(g213)
    c: Vertical(g215)
    c: Horizontal(g212,g141)
    c: Horizontal(g139,g141)
    c: Coincident(g216,g75)
    c: Vertical(g216)
    c: Symmetric(g205,g206,g216)
    c: PointOnObject(g212,g141)
    c: Tangent(g212,g217)
    c: PointOnObject(g217,g139)
    c: PointOnObject(g142,g217)
    c: Vertical(g142)
    c: Coincident(g218,g219)
    c: Coincident(g219,g220)
    c: Coincident(g220,g221)
    c: Coincident(g221,g218)
    c: Horizontal(g218)
    c: Horizontal(g220)
    c: Vertical(g219)
    c: Vertical(g221)
    c: PointOnObject(g218,g205)
    c: Coincident(g222,g223)
    c: Coincident(g223,g224)
    c: Coincident(g224,g225)
    c: Coincident(g225,g222)
    c: Horizontal(g222)
    c: Horizontal(g224)
    c: Vertical(g223)
    c: Vertical(g225)
    c: PointOnObject(g223,g206)
    c: Horizontal(g219,g224)
    c: Horizontal(g218,g222)
FEATURE [PartDesign::Body] Body
  Group = -> [Sketch]
  Origin = -> Origin
